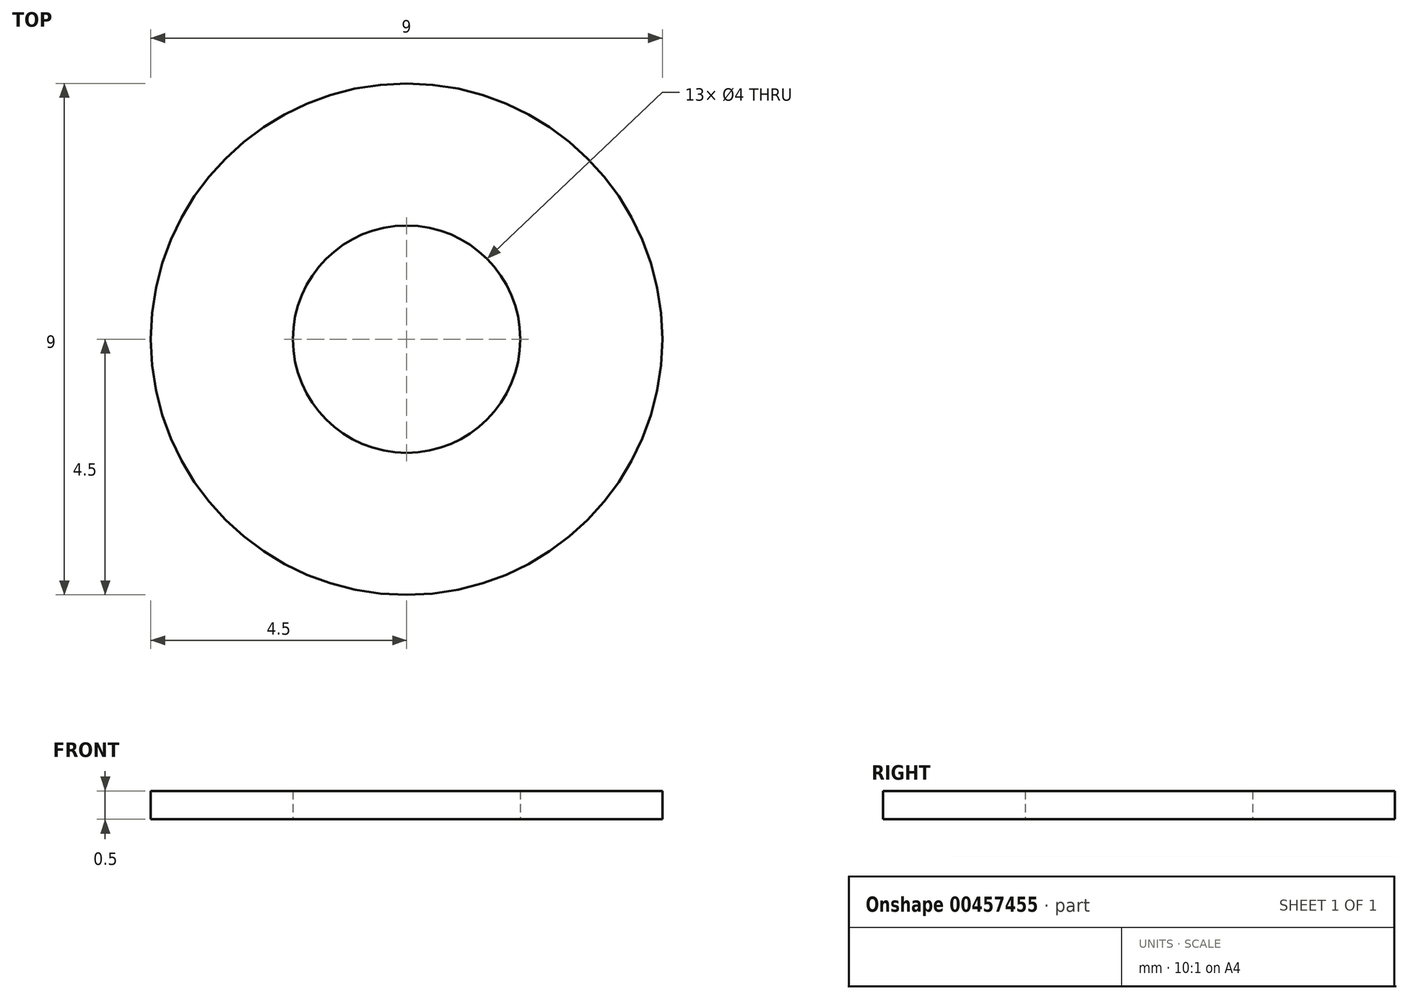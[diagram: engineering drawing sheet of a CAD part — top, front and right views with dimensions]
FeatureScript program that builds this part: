
annotation { "Feature Type Name" : "Feature", "Feature Type Description" : "" }
export const myFeature = defineFeature(function(context is Context, id is Id, definition is map)
    precondition{}
    {
        {
            var Q0;
            Q0=qCreatedBy(makeId("Top.planeOp"),FACE);
            var sketch = newSketch(context, id + "F0", { "sketchPlane" : qUnion([Q0])});
            skCircle(sketch, "E0", {"center": v(0, 0) * mm, "radius": 2 * mm});
            skCircle(sketch, "E1", {"center": v(0, 0) * mm, "radius": 4.5 * mm});
            skSolve(sketch);
        }
        {
            var Q0;
            Q0=makeQuery(id+"F0.imprint","IMPRINT",FACE,{"disambiguationData":[TD([[makeQuery(id+"F0.imprint","IMPRINT",EDGE,{"derivedFrom":sQuery(id+"F0.wireOp",EDGE,"E0")}),-1.0]])]});
            extrude(context, id + "F1", {"entities" : qUnion([Q0]), "depth" : .5 * mm});
        }
    });
